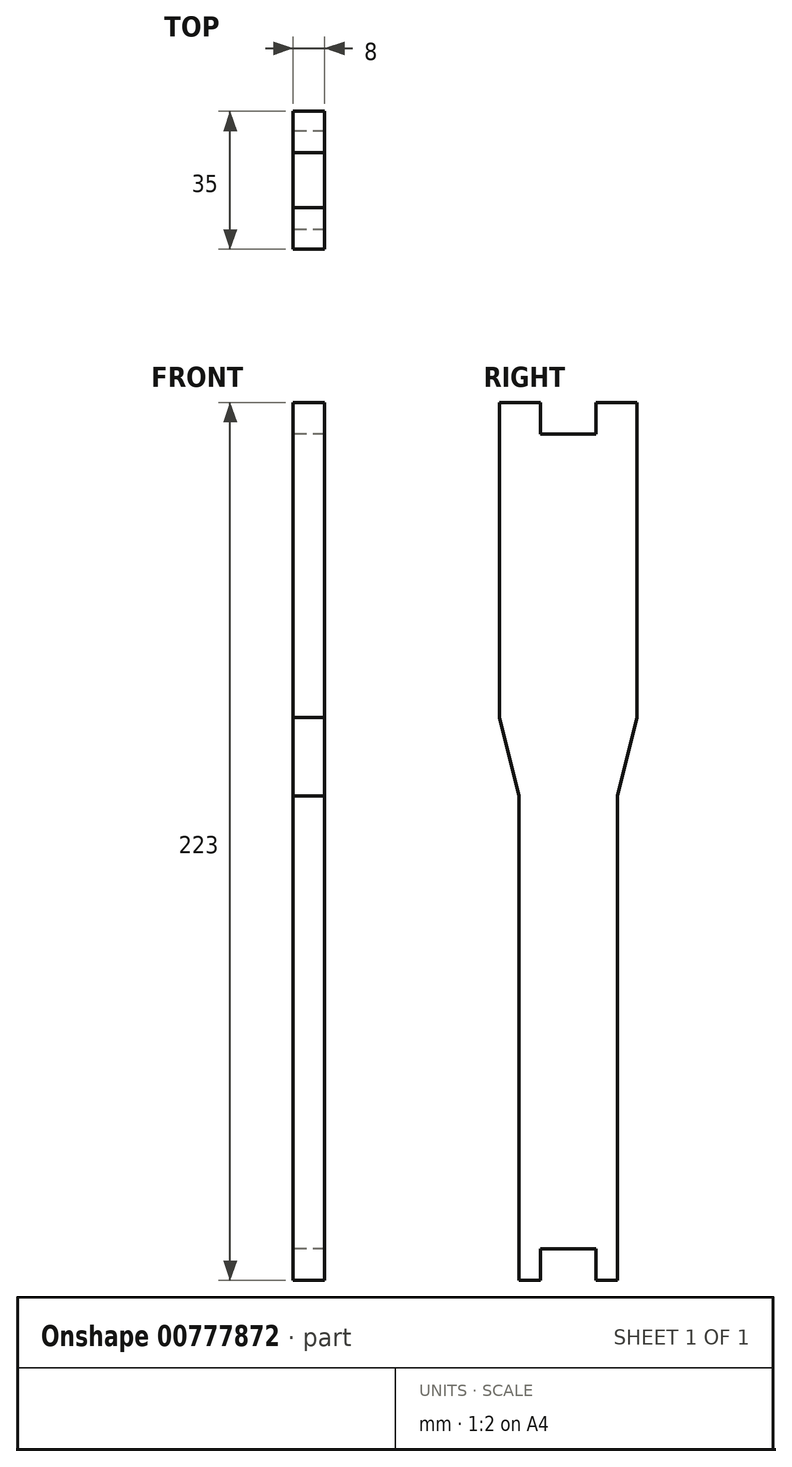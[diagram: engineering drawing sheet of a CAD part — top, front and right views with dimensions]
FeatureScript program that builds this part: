
annotation { "Feature Type Name" : "Feature", "Feature Type Description" : "" }
export const myFeature = defineFeature(function(context is Context, id is Id, definition is map)
    precondition{}
    {
        {
            var Q0;
            Q0=qCreatedBy(makeId("Right.planeOp"),FACE);
            var sketch = newSketch(context, id + "F0", { "sketchPlane" : qUnion([Q0])});
            skLineSegment(sketch, "E0", {"start": v(-7, 39.95) * mm, "end": v(7, 39.95) * mm});
            skLineSegment(sketch, "E1", {"start": v(7, 39.95) * mm, "end": v(7, 47.95) * mm});
            skLineSegment(sketch, "E2", {"start": v(7, 47.95) * mm, "end": v(17.5, 47.95) * mm});
            skLineSegment(sketch, "E3", {"start": v(-7, 39.95) * mm, "end": v(-7, 47.95) * mm});
            skLineSegment(sketch, "E4", {"start": v(-7, 47.95) * mm, "end": v(-17.5, 47.95) * mm});
            skLineSegment(sketch, "E5", {"start": v(-17.5, 47.95) * mm, "end": v(-17.5, -32.05) * mm});
            skLineSegment(sketch, "E6", {"start": v(17.5, 47.95) * mm, "end": v(17.5, -32.05) * mm});
            skLineSegment(sketch, "E7", {"start": v(-17.5, -32.05) * mm, "end": v(-12.5, -52.05) * mm});
            skLineSegment(sketch, "E8", {"start": v(17.5, -32.05) * mm, "end": v(12.5, -52.05) * mm});
            skLineSegment(sketch, "E9", {"start": v(12.5, -52.05) * mm, "end": v(12.5, -175.05) * mm});
            skLineSegment(sketch, "E10", {"start": v(12.5, -175.05) * mm, "end": v(7, -175.05) * mm});
            skLineSegment(sketch, "E11", {"start": v(7, -175.05) * mm, "end": v(7, -167.05) * mm});
            skLineSegment(sketch, "E12", {"start": v(7, -167.05) * mm, "end": v(-7, -167.05) * mm});
            skLineSegment(sketch, "E13", {"start": v(-7, -167.05) * mm, "end": v(-7, -175.05) * mm});
            skLineSegment(sketch, "E14", {"start": v(-7, -175.05) * mm, "end": v(-12.5, -175.05) * mm});
            skLineSegment(sketch, "E15", {"start": v(-12.5, -175.05) * mm, "end": v(-12.5, -52.05) * mm});
            skSolve(sketch);
        }
        {
            var Q0;
            Q0 = qSketchRegion(id + "F0", true);
            extrude(context, id + "F1", {"entities" : qUnion([Q0]), "endBound" : BoundingType.SYMMETRIC, "depth" : 8 * mm, "offsetDistance" : 25 * mm});
        }
    });
